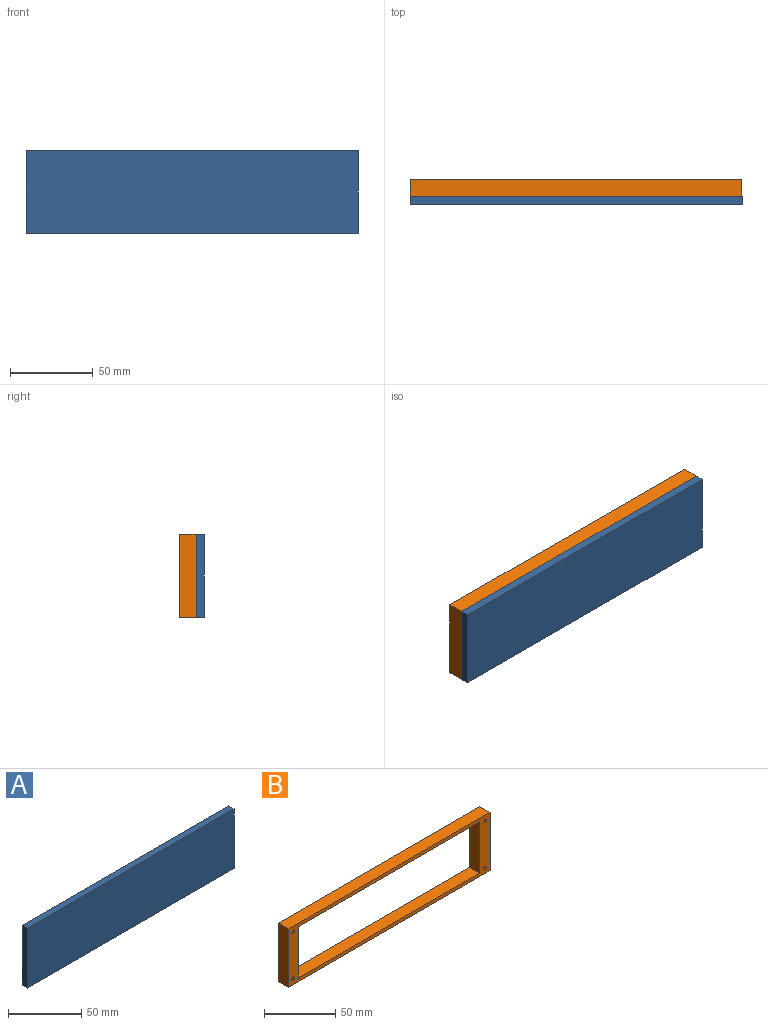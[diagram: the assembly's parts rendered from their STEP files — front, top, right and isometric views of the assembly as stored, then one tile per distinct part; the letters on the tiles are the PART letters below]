
ASSEMBLY  parts=2 mates=1
PART A: 6 faces, bbox 200x5x50 mm
  f0: plane 50x5mm, normal (-1,0,0), area 250mm2, adj f1,f3,f4,f5
  f1: plane 200x5mm, normal (0,0,-1), area 1000mm2, adj f0,f2,f4,f5
  f2: plane 50x5mm, normal (1,0,0), area 250mm2, adj f1,f3,f4,f5
  f3: plane 200x5mm, normal (0,0,1), area 1000mm2, adj f0,f2,f4,f5
  f4: plane 200x50mm, normal (0,-1,0), area 10000mm2, adj f0,f1,f2,f3
  f5: plane 200x50mm, normal (0,1,0), area 10000mm2, adj f0,f1,f2,f3
PART B: 18 faces, bbox 200x10x50 mm
  f0: plane 50x10mm, normal (-1,0,0), area 500mm2, adj f1,f3,f4,f5
  f1: plane 200x10mm, normal (0,0,-1), area 2000mm2, adj f0,f2,f4,f5
  f2: plane 50x10mm, normal (1,0,0), area 500mm2, adj f1,f3,f4,f5
  f3: plane 200x10mm, normal (0,0,1), area 2000mm2, adj f0,f2,f4,f5
  f4: plane 200x50mm, normal (0,-1,0), area 2060.4mm2, adj f0,f1,f2,f3,f6,f7,f8,f9
  f5: plane 200x50mm, normal (0,1,0), area 1938.1mm2, adj f0,f1,f2,f3,f6,f7,f8,f9
  f6: plane 44x10mm, normal (1,0,0), area 440mm2, adj f4,f5,f7,f9
  f7: plane 180x10mm, normal (0,0,1), area 1800mm2, adj f4,f5,f6,f8
  f8: plane 44x10mm, normal (-1,0,0), area 440mm2, adj f4,f5,f7,f9
  f9: plane 180x10mm, normal (0,0,-1), area 1800mm2, adj f4,f5,f6,f8
  f10: cylinder r=1.25mm len=7.89mm, axis (0,1,0), area 62mm2, adj f4,f11
  f11: cone r=1.25mm half-angle=45deg, axis (0,1,0), area 43.2mm2, adj f5,f10
  f12: cylinder r=1.25mm len=7.89mm, axis (0,1,0), area 62mm2, adj f4,f13
  f13: cone r=1.25mm half-angle=45deg, axis (0,1,0), area 43.2mm2, adj f5,f12
  f14: cylinder r=1.25mm len=7.89mm, axis (0,1,0), area 62mm2, adj f4,f15
  f15: cone r=1.25mm half-angle=45deg, axis (0,1,0), area 43.2mm2, adj f5,f14
  f16: cylinder r=1.25mm len=7.89mm, axis (0,1,0), area 62mm2, adj f4,f17
  f17: cone r=1.25mm half-angle=45deg, axis (0,1,0), area 43.2mm2, adj f5,f16
PLACE A rot(axis=(1,0,0),180deg) t=(-8.97,-15,-78.28)mm
PLACE B at identity fixed
MATE fastened A.f4 <-> B.f4  axis (0,1,0) through (100.38,-10,-23.07)mm
